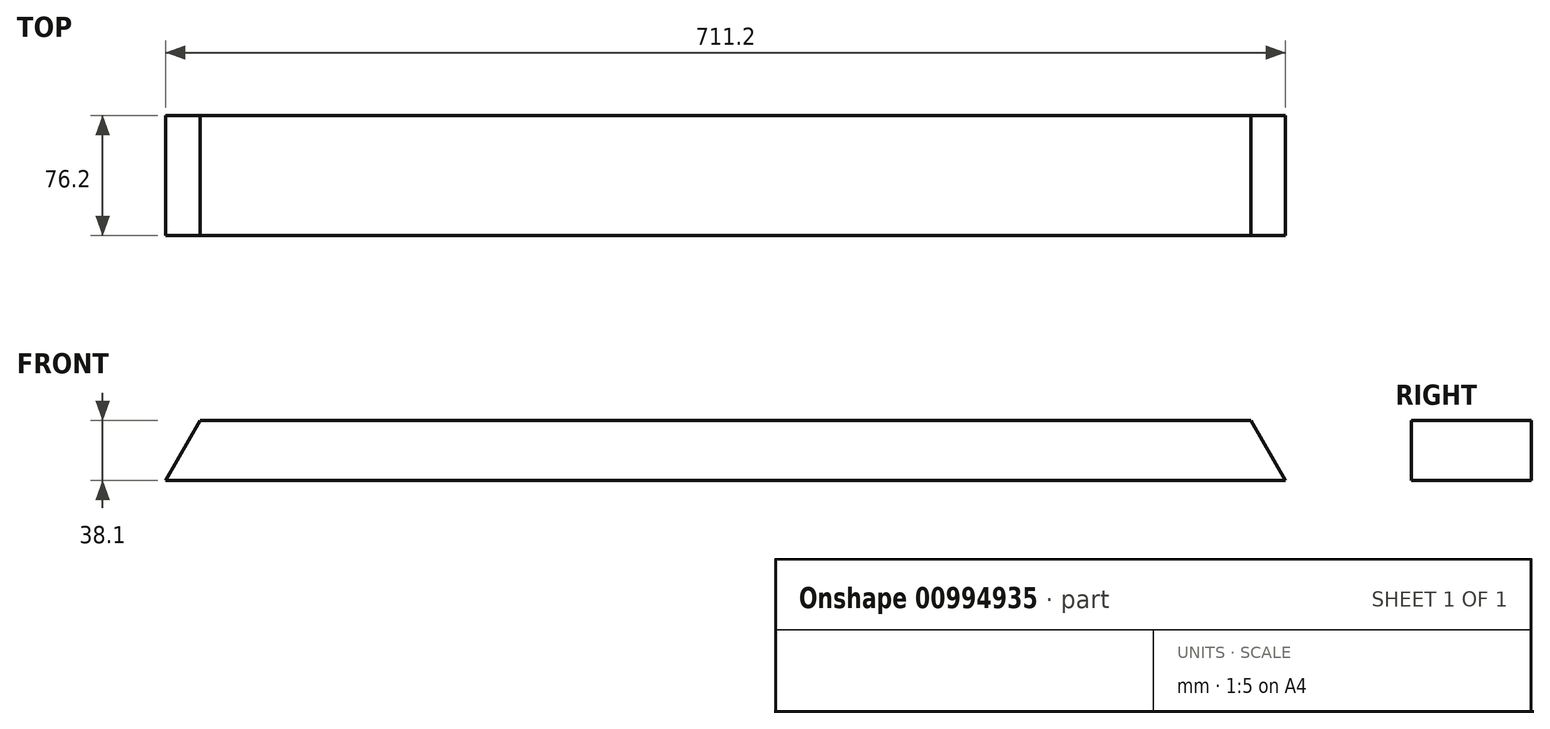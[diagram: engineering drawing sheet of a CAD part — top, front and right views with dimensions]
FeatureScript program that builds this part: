
annotation { "Feature Type Name" : "Feature", "Feature Type Description" : "" }
export const myFeature = defineFeature(function(context is Context, id is Id, definition is map)
    precondition{}
    {
        {
            var Q0;
            Q0=qCreatedBy(makeId("Front.planeOp"),FACE);
            var sketch = newSketch(context, id + "F0", { "sketchPlane" : qUnion([Q0])});
            skLineSegment(sketch, "E0", {"start": v(-355.6, 0) * mm, "end": v(355.6, 0) * mm});
            skLineSegment(sketch, "E1", {"start": v(-355.6, 0) * mm, "end": v(-333.6, 38.1) * mm});
            skLineSegment(sketch, "E2", {"start": v(-333.6, 38.1) * mm, "end": v(333.6, 38.1) * mm});
            skLineSegment(sketch, "E3", {"start": v(333.6, 38.1) * mm, "end": v(355.6, 0) * mm});
            skSolve(sketch);
        }
        {
            var Q0;
            Q0=makeQuery(id+"F0.imprint","IMPRINT",FACE,{"disambiguationData":[TD([[makeQuery(id+"F0.imprint","IMPRINT",EDGE,{"derivedFrom":sQuery(id+"F0.wireOp",EDGE,"E0")}),1.0]])]});
            extrude(context, id + "F1", {"entities" : qUnion([Q0]), "oppositeDirection" : true, "depth" : 76.2 * mm, "offsetDistance" : 25.4 * mm});
        }
    });
